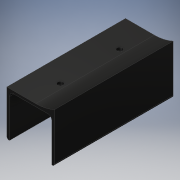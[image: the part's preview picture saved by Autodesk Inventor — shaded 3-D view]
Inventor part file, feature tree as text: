
AUTODESK INVENTOR PART (.ipt)
format: ipt  version: 2019.4 (Build 234330000, 330)  size: 133,120 bytes
history: native  units: mm
features: fillet x2, sketch x2, extrude x1, hole x1
ambient origin geometry x8: Origin, YZ Plane, XZ Plane, XY Plane, X Axis, Y Axis, Z Axis, Center Point
bodies: Solid1 (feature_tree)
feature tree (6):
  extrude  "Extrusion1"  Depth=40.0mm
  hole  "Hole1"  [1 undecoded]
  fillet  "Fillet1"  Radius=2.5mm
  fillet  "Fillet2"  Radius=2.5mm
  sketch  "Sketch1"  dims[d0=40.0mm d1=40.0mm]
  sketch  "Sketch2"  dims[d2=2.5mm d3=42.5mm d4=2.5mm d5=2.5mm d6=27.244mm d7=3.984mm d8=41.559mm d9=112.1mm d10=0.0mm d11=5.0mm d12=6.0mm d13=4.0mm d14=2.0mm d15=90.0deg d16=8.0mm d17=20.594885mm d18=4.0mm d19=2.0mm]
note: 1 required parameter value undecoded (feature->parameter linkage not recoverable at this tier; creation-order binding heuristic only, values carry confidence <= 0.55)
